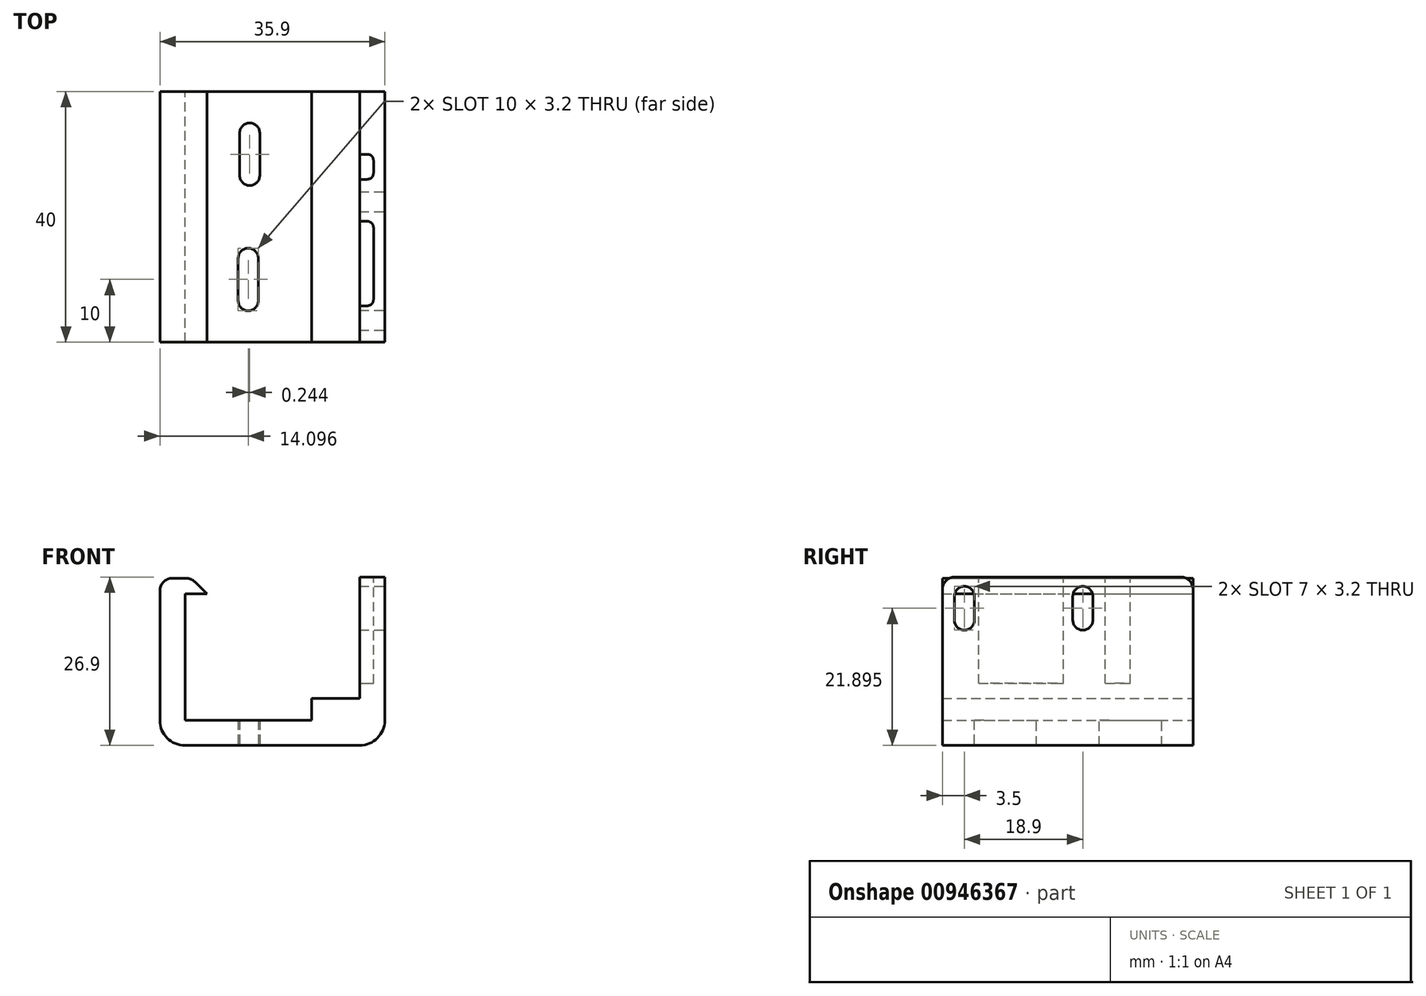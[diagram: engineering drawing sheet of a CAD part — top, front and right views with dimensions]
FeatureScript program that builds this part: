
annotation { "Feature Type Name" : "Feature", "Feature Type Description" : "" }
export const myFeature = defineFeature(function(context is Context, id is Id, definition is map)
    precondition{}
    {
        {
            var Q0;
            Q0=qCreatedBy(makeId("Front.planeOp"),FACE);
            var sketch = newSketch(context, id + "F0", { "sketchPlane" : qUnion([Q0])});
            skLineSegment(sketch, "E0", {"start": v(21.06, -3.37) * mm, "end": v(17.06, -3.37) * mm});
            skLineSegment(sketch, "E1", {"start": v(17.06, -3.37) * mm, "end": v(17.06, -22.77) * mm});
            skLineSegment(sketch, "E2", {"start": v(-10.84, -26.27) * mm, "end": v(-10.84, -6.07) * mm});
            skLineSegment(sketch, "E3", {"start": v(-10.84, -6.07) * mm, "end": v(-7.34, -6.07) * mm});
            skLineSegment(sketch, "E4", {"start": v(-7.34, -6.07) * mm, "end": v(-9.84, -3.57) * mm});
            skLineSegment(sketch, "E5", {"start": v(-9.84, -3.57) * mm, "end": v(-14.84, -3.57) * mm});
            skLineSegment(sketch, "E6", {"start": v(-14.84, -3.57) * mm, "end": v(-14.84, -30.27) * mm});
            skLineSegment(sketch, "E7", {"start": v(-14.84, -30.27) * mm, "end": v(21.06, -30.27) * mm});
            skLineSegment(sketch, "E8", {"start": v(21.06, -30.27) * mm, "end": v(21.06, -3.37) * mm});
            skLineSegment(sketch, "E9", {"start": v(17.06, -22.77) * mm, "end": v(9.36, -22.77) * mm});
            skLineSegment(sketch, "E10", {"start": v(9.36, -22.77) * mm, "end": v(9.36, -26.27) * mm});
            skLineSegment(sketch, "E11", {"start": v(9.36, -26.27) * mm, "end": v(-10.84, -26.27) * mm});
            skSolve(sketch);
        }
        {
            var Q0;
            Q0=qSketchRegion(id+"F0",true);
            extrude(context, id + "F1", {"entities" : qUnion([Q0]), "depth" : 40 * mm, "offsetDistance" : 25 * mm});
        }
        {
            var Q0;
            Q0=makeQuery(id+"F1.opExtrude","SWEPT_EDGE",EDGE,{"disambiguationData":[OSD([sQuery(id+"F0.wireOp",EDGE,"E6"),sQuery(id+"F0.wireOp",EDGE,"E7")])]});
            var Q1;
            Q1=makeQuery(id+"F1.opExtrude","SWEPT_EDGE",EDGE,{"disambiguationData":[OSD([sQuery(id+"F0.wireOp",EDGE,"E7"),sQuery(id+"F0.wireOp",EDGE,"E8")])]});
            fillet(context, id + "F2", {"entities" : qUnion([Q0, Q1]), "radius" : 4 * mm, "tangentPropagation" : true, "allowEdgeOverflow" : false});
        }
        {
            var Q0;
            Q0=makeQuery(id+"F1.opExtrude","SWEPT_EDGE",EDGE,{"disambiguationData":[OSD([sQuery(id+"F0.wireOp",EDGE,"E4"),sQuery(id+"F0.wireOp",EDGE,"E5")])]});
            fillet(context, id + "F3", {"entities" : qUnion([Q0]), "radius" : 2 * mm, "tangentPropagation" : true, "allowEdgeOverflow" : false});
        }
        {
            var Q0;
            Q0=makeQuery(id+"F1.opExtrude","SWEPT_FACE",FACE,{"disambiguationData":[OSD([sQuery(id+"F0.wireOp",EDGE,"E8")])]});
            var sketch = newSketch(context, id + "F4", { "sketchPlane" : qUnion([Q0])});
            skLineSegment(sketch, "E12.bottom", {"start": v(-19.2, -4.87) * mm, "end": v(-16, -4.87) * mm});
            skLineSegment(sketch, "E12.top", {"start": v(-19.2, -11.87) * mm, "end": v(-16, -11.87) * mm});
            skLineSegment(sketch, "E12.left", {"start": v(-19.2, -4.87) * mm, "end": v(-19.2, -11.87) * mm});
            skLineSegment(sketch, "E12.right", {"start": v(-16, -4.87) * mm, "end": v(-16, -11.87) * mm});
            skLineSegment(sketch, "E13.bottom", {"start": v(-34.9, -4.87) * mm, "end": v(-38.1, -4.87) * mm});
            skLineSegment(sketch, "E13.top", {"start": v(-34.9, -11.87) * mm, "end": v(-38.1, -11.87) * mm});
            skLineSegment(sketch, "E13.left", {"start": v(-34.9, -4.87) * mm, "end": v(-34.9, -11.87) * mm});
            skLineSegment(sketch, "E13.right", {"start": v(-38.1, -4.87) * mm, "end": v(-38.1, -11.87) * mm});
            skSolve(sketch);
        }
        {
            var Q0;
            Q0=qSketchRegion(id+"F4",true);
            extrude(context, id + "F5", {"entities" : qUnion([Q0]), "operationType" : NewBodyOperationType.REMOVE, "endBound" : BoundingType.UP_TO_NEXT, "oppositeDirection" : true, "depth" : 25 * mm, "offsetDistance" : 25 * mm});
        }
        {
            var Q0;
            Q0=makeQuery(id+"F5.boolean.opBoolean","COPY",EDGE,{"derivedFrom":makeQuery(id+"F5.opExtrude","SWEPT_EDGE",EDGE,{"disambiguationData":[OSD([sQuery(id+"F4.wireOp",EDGE,"E12.bottom"),sQuery(id+"F4.wireOp",EDGE,"E12.left")])]})});
            var Q1;
            Q1=makeQuery(id+"F5.boolean.opBoolean","COPY",EDGE,{"derivedFrom":makeQuery(id+"F5.opExtrude","SWEPT_EDGE",EDGE,{"disambiguationData":[OSD([sQuery(id+"F4.wireOp",EDGE,"E12.bottom"),sQuery(id+"F4.wireOp",EDGE,"E12.right")])]})});
            var Q2;
            Q2=makeQuery(id+"F5.boolean.opBoolean","COPY",EDGE,{"derivedFrom":makeQuery(id+"F5.opExtrude","SWEPT_EDGE",EDGE,{"disambiguationData":[OSD([sQuery(id+"F4.wireOp",EDGE,"E12.top"),sQuery(id+"F4.wireOp",EDGE,"E12.right")])]})});
            var Q3;
            Q3=makeQuery(id+"F5.boolean.opBoolean","COPY",EDGE,{"derivedFrom":makeQuery(id+"F5.opExtrude","SWEPT_EDGE",EDGE,{"disambiguationData":[OSD([sQuery(id+"F4.wireOp",EDGE,"E12.top"),sQuery(id+"F4.wireOp",EDGE,"E12.left")])]})});
            var Q4;
            Q4=makeQuery(id+"F5.boolean.opBoolean","COPY",EDGE,{"derivedFrom":makeQuery(id+"F5.opExtrude","SWEPT_EDGE",EDGE,{"disambiguationData":[OSD([sQuery(id+"F4.wireOp",EDGE,"E13.top"),sQuery(id+"F4.wireOp",EDGE,"E13.right")])]})});
            var Q5;
            Q5=makeQuery(id+"F5.boolean.opBoolean","COPY",EDGE,{"derivedFrom":makeQuery(id+"F5.opExtrude","SWEPT_EDGE",EDGE,{"disambiguationData":[OSD([sQuery(id+"F4.wireOp",EDGE,"E13.top"),sQuery(id+"F4.wireOp",EDGE,"E13.left")])]})});
            var Q6;
            Q6=makeQuery(id+"F5.boolean.opBoolean","COPY",EDGE,{"derivedFrom":makeQuery(id+"F5.opExtrude","SWEPT_EDGE",EDGE,{"disambiguationData":[OSD([sQuery(id+"F4.wireOp",EDGE,"E13.bottom"),sQuery(id+"F4.wireOp",EDGE,"E13.left")])]})});
            var Q7;
            Q7=makeQuery(id+"F5.boolean.opBoolean","COPY",EDGE,{"derivedFrom":makeQuery(id+"F5.opExtrude","SWEPT_EDGE",EDGE,{"disambiguationData":[OSD([sQuery(id+"F4.wireOp",EDGE,"E13.bottom"),sQuery(id+"F4.wireOp",EDGE,"E13.right")])]})});
            fillet(context, id + "F6", {"entities" : qUnion([Q0, Q1, Q2, Q3, Q4, Q5, Q6, Q7]), "radius" : 1.6 * mm, "tangentPropagation" : true, "allowEdgeOverflow" : false});
        }
        {
            var Q0;
            Q0=makeQuery(id+"F1.opExtrude","SWEPT_FACE",FACE,{"disambiguationData":[OSD([sQuery(id+"F0.wireOp",EDGE,"E7")])]});
            var sketch = newSketch(context, id + "F7", { "sketchPlane" : qUnion([Q0])});
            skLineSegment(sketch, "E14.bottom", {"start": v(-2.1, 5) * mm, "end": v(-2.1, 15) * mm});
            skLineSegment(sketch, "E14.top", {"start": v(1.1, 5) * mm, "end": v(1.1, 15) * mm});
            skLineSegment(sketch, "E14.left", {"start": v(-2.1, 5) * mm, "end": v(1.1, 5) * mm});
            skLineSegment(sketch, "E14.right", {"start": v(-2.1, 15) * mm, "end": v(1.1, 15) * mm});
            skLineSegment(sketch, "E15.bottom", {"start": v(-2.34, 25) * mm, "end": v(-2.34, 35) * mm});
            skLineSegment(sketch, "E15.top", {"start": v(0.86, 25) * mm, "end": v(0.86, 35) * mm});
            skLineSegment(sketch, "E15.left", {"start": v(-2.34, 25) * mm, "end": v(0.86, 25) * mm});
            skLineSegment(sketch, "E15.right", {"start": v(-2.34, 35) * mm, "end": v(0.86, 35) * mm});
            skSolve(sketch);
        }
        {
            var Q0;
            Q0=qSketchRegion(id+"F7",true);
            extrude(context, id + "F8", {"entities" : qUnion([Q0]), "operationType" : NewBodyOperationType.REMOVE, "endBound" : BoundingType.UP_TO_NEXT, "oppositeDirection" : true, "depth" : 25 * mm, "offsetDistance" : 25 * mm});
        }
        {
            var Q0;
            Q0=makeQuery(id+"F8.boolean.opBoolean","COPY",EDGE,{"derivedFrom":makeQuery(id+"F8.opExtrude","SWEPT_EDGE",EDGE,{"disambiguationData":[OSD([sQuery(id+"F7.wireOp",EDGE,"E15.top"),sQuery(id+"F7.wireOp",EDGE,"E15.right")])]})});
            var Q1;
            Q1=makeQuery(id+"F8.boolean.opBoolean","COPY",EDGE,{"derivedFrom":makeQuery(id+"F8.opExtrude","SWEPT_EDGE",EDGE,{"disambiguationData":[OSD([sQuery(id+"F7.wireOp",EDGE,"E15.bottom"),sQuery(id+"F7.wireOp",EDGE,"E15.right")])]})});
            var Q2;
            Q2=makeQuery(id+"F8.boolean.opBoolean","COPY",EDGE,{"derivedFrom":makeQuery(id+"F8.opExtrude","SWEPT_EDGE",EDGE,{"disambiguationData":[OSD([sQuery(id+"F7.wireOp",EDGE,"E14.bottom"),sQuery(id+"F7.wireOp",EDGE,"E14.right")])]})});
            var Q3;
            Q3=makeQuery(id+"F8.boolean.opBoolean","COPY",EDGE,{"derivedFrom":makeQuery(id+"F8.opExtrude","SWEPT_EDGE",EDGE,{"disambiguationData":[OSD([sQuery(id+"F7.wireOp",EDGE,"E14.top"),sQuery(id+"F7.wireOp",EDGE,"E14.right")])]})});
            var Q4;
            Q4=makeQuery(id+"F8.boolean.opBoolean","COPY",EDGE,{"derivedFrom":makeQuery(id+"F8.opExtrude","SWEPT_EDGE",EDGE,{"disambiguationData":[OSD([sQuery(id+"F7.wireOp",EDGE,"E15.top"),sQuery(id+"F7.wireOp",EDGE,"E15.left")])]})});
            var Q5;
            Q5=makeQuery(id+"F8.boolean.opBoolean","COPY",EDGE,{"derivedFrom":makeQuery(id+"F8.opExtrude","SWEPT_EDGE",EDGE,{"disambiguationData":[OSD([sQuery(id+"F7.wireOp",EDGE,"E14.top"),sQuery(id+"F7.wireOp",EDGE,"E14.left")])]})});
            var Q6;
            Q6=makeQuery(id+"F8.boolean.opBoolean","COPY",EDGE,{"derivedFrom":makeQuery(id+"F8.opExtrude","SWEPT_EDGE",EDGE,{"disambiguationData":[OSD([sQuery(id+"F7.wireOp",EDGE,"E15.bottom"),sQuery(id+"F7.wireOp",EDGE,"E15.left")])]})});
            var Q7;
            Q7=makeQuery(id+"F8.boolean.opBoolean","COPY",EDGE,{"derivedFrom":makeQuery(id+"F8.opExtrude","SWEPT_EDGE",EDGE,{"disambiguationData":[OSD([sQuery(id+"F7.wireOp",EDGE,"E14.bottom"),sQuery(id+"F7.wireOp",EDGE,"E14.left")])]})});
            fillet(context, id + "F9", {"entities" : qUnion([Q0, Q1, Q2, Q3, Q4, Q5, Q6, Q7]), "radius" : 1.6 * mm, "tangentPropagation" : true, "allowEdgeOverflow" : false});
        }
        {
            var Q0;
            Q0=makeQuery(id+"F1.opExtrude","SWEPT_FACE",FACE,{"disambiguationData":[OSD([sQuery(id+"F0.wireOp",EDGE,"E0")])]});
            var sketch = newSketch(context, id + "F10", { "sketchPlane" : qUnion([Q0])});
            skLineSegment(sketch, "E16.bottom", {"start": v(17.06, -10) * mm, "end": v(19.26, -10) * mm});
            skLineSegment(sketch, "E16.top", {"start": v(17.06, -14) * mm, "end": v(19.26, -14) * mm});
            skLineSegment(sketch, "E16.left", {"start": v(17.06, -10) * mm, "end": v(17.06, -14) * mm});
            skLineSegment(sketch, "E16.right", {"start": v(19.26, -10) * mm, "end": v(19.26, -14) * mm});
            skLineSegment(sketch, "E17.bottom", {"start": v(17.06, -20.7) * mm, "end": v(19.26, -20.7) * mm});
            skLineSegment(sketch, "E17.top", {"start": v(17.06, -34.2) * mm, "end": v(19.26, -34.2) * mm});
            skLineSegment(sketch, "E17.left", {"start": v(17.06, -20.7) * mm, "end": v(17.06, -34.2) * mm});
            skLineSegment(sketch, "E17.right", {"start": v(19.26, -20.7) * mm, "end": v(19.26, -34.2) * mm});
            skSolve(sketch);
        }
        {
            var Q0;
            Q0=qSketchRegion(id+"F10",true);
            extrude(context, id + "F11", {"entities" : qUnion([Q0]), "operationType" : NewBodyOperationType.REMOVE, "oppositeDirection" : true, "depth" : 17 * mm, "offsetDistance" : 25 * mm});
        }
        {
            var Q0;
            Q0=makeQuery(id+"F1.opExtrude","CAP_EDGE",EDGE,{"disambiguationData":[OSD([sQuery(id+"F0.wireOp",EDGE,"E0")])],"isStart":false});
            var Q1;
            Q1=makeQuery(id+"F1.opExtrude","CAP_EDGE",EDGE,{"disambiguationData":[OSD([sQuery(id+"F0.wireOp",EDGE,"E0")])],"isStart":true});
            fillet(context, id + "F12", {"entities" : qUnion([Q0, Q1]), "radius" : 2 * mm, "tangentPropagation" : true, "allowEdgeOverflow" : false});
        }
        {
            var Q0;
            Q0=makeQuery(id+"F11.boolean.opBoolean","COPY",EDGE,{"derivedFrom":makeQuery(id+"F11.opExtrude","SWEPT_EDGE",EDGE,{"disambiguationData":[OSD([sQuery(id+"F10.wireOp",EDGE,"E16.top"),sQuery(id+"F10.wireOp",EDGE,"E16.right")])]})});
            var Q1;
            Q1=makeQuery(id+"F11.boolean.opBoolean","COPY",EDGE,{"derivedFrom":makeQuery(id+"F11.opExtrude","SWEPT_EDGE",EDGE,{"disambiguationData":[OSD([sQuery(id+"F10.wireOp",EDGE,"E16.bottom"),sQuery(id+"F10.wireOp",EDGE,"E16.right")])]})});
            var Q2;
            Q2=makeQuery(id+"F11.boolean.opBoolean","COPY",EDGE,{"derivedFrom":makeQuery(id+"F11.opExtrude","SWEPT_EDGE",EDGE,{"disambiguationData":[OSD([sQuery(id+"F10.wireOp",EDGE,"E17.bottom"),sQuery(id+"F10.wireOp",EDGE,"E17.right")])]})});
            var Q3;
            Q3=makeQuery(id+"F11.boolean.opBoolean","COPY",EDGE,{"derivedFrom":makeQuery(id+"F11.opExtrude","SWEPT_EDGE",EDGE,{"disambiguationData":[OSD([sQuery(id+"F10.wireOp",EDGE,"E17.top"),sQuery(id+"F10.wireOp",EDGE,"E17.right")])]})});
            fillet(context, id + "F13", {"entities" : qUnion([Q0, Q1, Q2, Q3]), "radius" : 1 * mm, "tangentPropagation" : true, "allowEdgeOverflow" : false});
        }
        {
            var Q0;
            Q0=makeQuery(id+"F1.opExtrude","SWEPT_EDGE",EDGE,{"disambiguationData":[OSD([sQuery(id+"F0.wireOp",EDGE,"E5"),sQuery(id+"F0.wireOp",EDGE,"E6")])]});
            fillet(context, id + "F14", {"entities" : qUnion([Q0]), "radius" : 2 * mm, "tangentPropagation" : true, "allowEdgeOverflow" : false});
        }
    });
